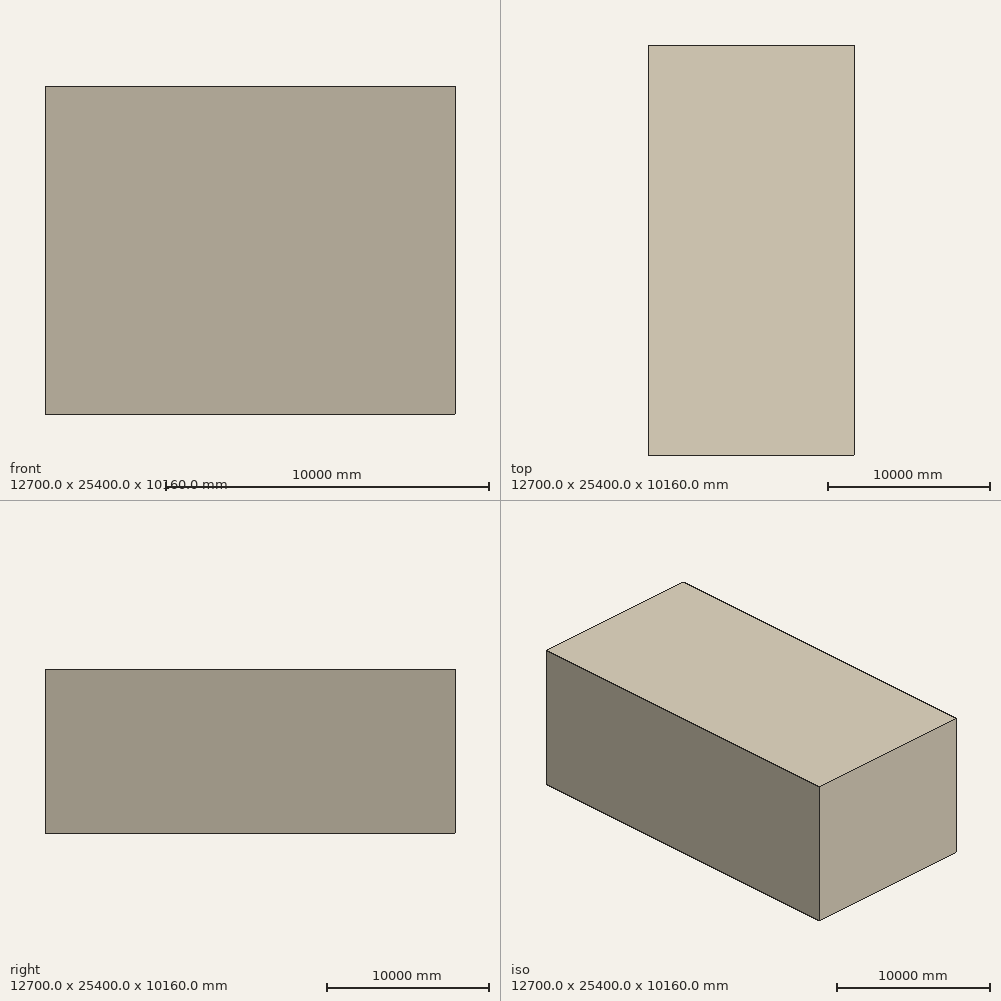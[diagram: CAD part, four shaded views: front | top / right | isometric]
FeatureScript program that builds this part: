
annotation { "Feature Type Name" : "Feature", "Feature Type Description" : "" }
export const myFeature = defineFeature(function(context is Context, id is Id, definition is map)
    precondition{}
    {
        {
            var Q0;
            Q0=qCreatedBy(makeId("Top.planeOp"),FACE);
            var sketch = newSketch(context, id + "F0", { "sketchPlane" : qUnion([Q0])});
            skLineSegment(sketch, "E0.bottom", {"start": v(0, 0) * mm, "end": v(12700, 0) * mm});
            skLineSegment(sketch, "E0.top", {"start": v(0, 25400) * mm, "end": v(12700, 25400) * mm});
            skLineSegment(sketch, "E0.left", {"start": v(0, 0) * mm, "end": v(0, 25400) * mm});
            skLineSegment(sketch, "E0.right", {"start": v(12700, 0) * mm, "end": v(12700, 25400) * mm});
            skSolve(sketch);
        }
        {
            var Q0;
            Q0 = qSketchRegion(id + "F0", true);
            extrude(context, id + "F1", {"entities" : qUnion([Q0]), "depth" : 10160 * mm, "offsetDistance" : 25.4 * mm});
        }
    });
